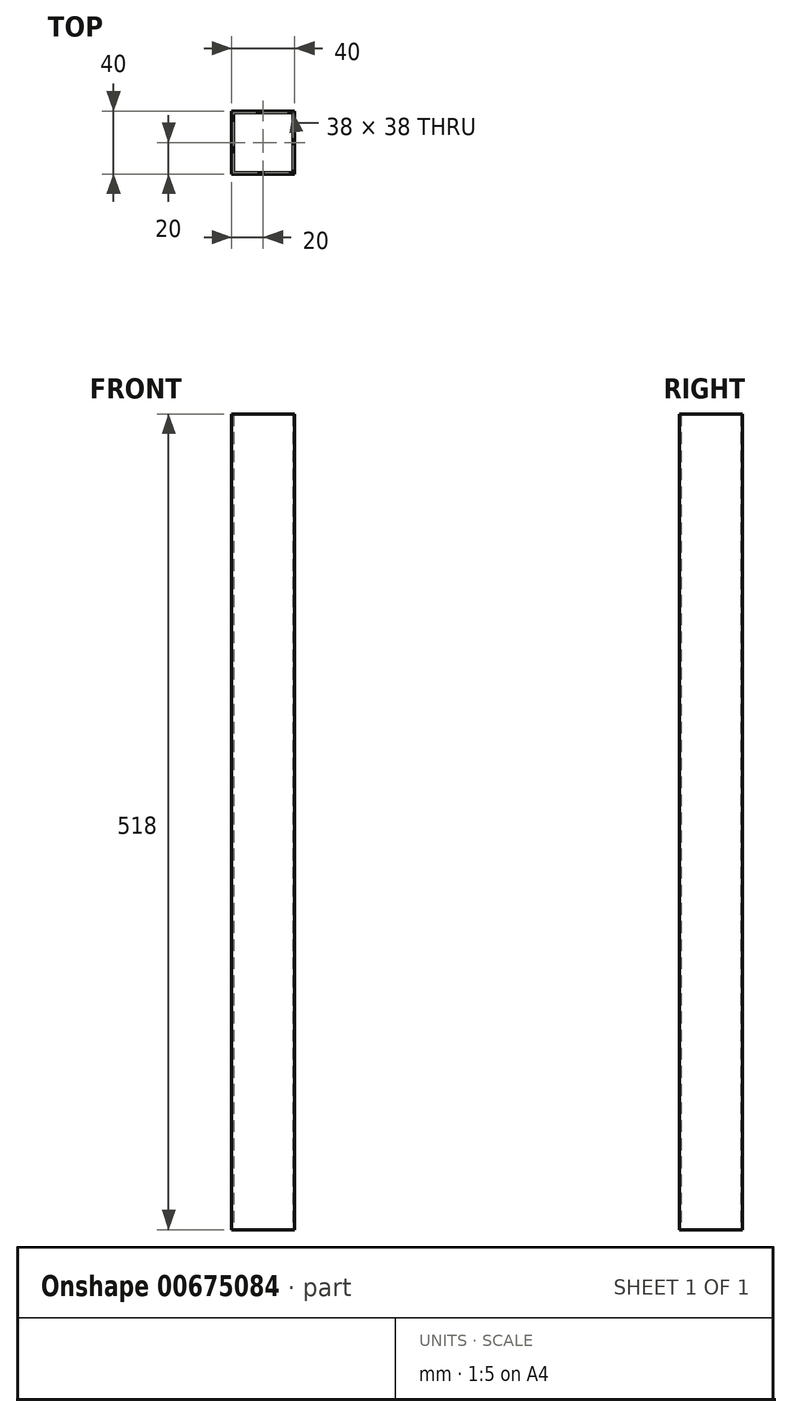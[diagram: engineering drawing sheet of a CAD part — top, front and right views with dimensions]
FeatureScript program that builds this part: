
annotation { "Feature Type Name" : "Feature", "Feature Type Description" : "" }
export const myFeature = defineFeature(function(context is Context, id is Id, definition is map)
    precondition{}
    {
        {
            var Q0;
            Q0=qCreatedBy(makeId("Top.planeOp"),FACE);
            var sketch = newSketch(context, id + "F0", { "sketchPlane" : qUnion([Q0])});
            skLineSegment(sketch, "E0.bottom", {"start": v(19, 19) * mm, "end": v(-19, 19) * mm});
            skLineSegment(sketch, "E0.top", {"start": v(19, -19) * mm, "end": v(-19, -19) * mm});
            skLineSegment(sketch, "E0.left", {"start": v(19, 19) * mm, "end": v(19, -19) * mm});
            skLineSegment(sketch, "E0.right", {"start": v(-19, 19) * mm, "end": v(-19, -19) * mm});
            skPoint(sketch, "E0.middle", {"position": v(0, 0) * mm});
            skLineSegment(sketch, "E1.bottom", {"start": v(20, 20) * mm, "end": v(-20, 20) * mm});
            skLineSegment(sketch, "E1.top", {"start": v(20, -20) * mm, "end": v(-20, -20) * mm});
            skLineSegment(sketch, "E1.left", {"start": v(20, 20) * mm, "end": v(20, -20) * mm});
            skLineSegment(sketch, "E1.right", {"start": v(-20, 20) * mm, "end": v(-20, -20) * mm});
            skSolve(sketch);
        }
        {
            var Q0;
            Q0=makeQuery(id+"F0.imprint","IMPRINT",FACE,{"disambiguationData":[TD([[makeQuery(id+"F0.imprint","IMPRINT",EDGE,{"derivedFrom":sQuery(id+"F0.wireOp",EDGE,"E0.bottom")}),-1.0]])]});
            extrude(context, id + "F1", {"entities" : qUnion([Q0]), "depth" : (520 - 2) * mm, "offsetDistance" : 25 * mm});
        }
    });
